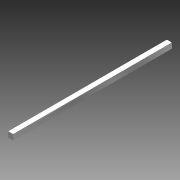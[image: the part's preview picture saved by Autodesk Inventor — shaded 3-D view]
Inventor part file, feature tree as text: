
AUTODESK INVENTOR PART (.ipt)
format: ipt  version: 2012 (Build 160160000, 160)  size: 119,808 bytes
history: native  units: in
note: dims shown in document units (in); Inventor stores cm internally (conversion verified against a paired STEP export)
features: other x1, imported_body x1, plane x1, split x1
ambient origin geometry x8: Origin, YZ Plane, XZ Plane, XY Plane, X Axis, Y Axis, Z Axis, Center Point
feature tree (4):
  parser-record x1  (decoder bookkeeping rows leaked as tree rows — omitted from the tree; the rows remain in map.json)
  imported_body  "Base1"
  plane  "Work Plane1"
  split  "Split1"
